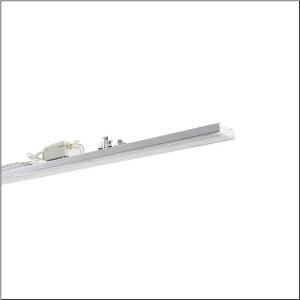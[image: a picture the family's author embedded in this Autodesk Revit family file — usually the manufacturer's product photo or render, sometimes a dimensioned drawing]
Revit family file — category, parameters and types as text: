
# Revit family: licross_r__21_recessed_mo_52tl12de45xg_f928
name_source: partatom
category: Lighting Fixtures
units: mm (PartAtom-declared; Revit-internal decimal feet)

## family parameters
Cut with Voids When Loaded = No
Host = Face
Light Source = No
Part Type = Normal
Room Calculation Point = No
Round Connector Dimension = Use Diameter
Shared = No

## types (1)
- --- (1 x LED, 5140 lm, 29.9 W, 4000K)
    Apparent Load = 30 VA
    CIE Flux Codes = 72 92 99 100 100
    Color Rendering = 80
    Color Temperature = 4000K
    Default Elevation = 1800 mm
    Description = Licross® 21 Recessed MO, luminaire insert, of sheet steel, galvanised, coil coated, white, length: 750mm, width: 66mm, height: 67mm, LED rated luminous flux: 5.140lm, light colour: 840, control gear: DALI 2, with plug, 5-pole, with phase selection, mains connection: 220..240V, AC, 50/60Hz, rated input power: 30W, halogen-free wiring, primary light control with lens, of plastic, primary optical cover: cover, of PMMA, light emission: direct distribution, primary light characteristic: symmetric, protection rating (complete): IP40, insulation class (complete): insulation class I (protective earthing), certification: CE, ENEC, VDE, UKCA, protection symbol: D if used in an environment without relevant dust loads with corresponding accessories, impact resistance: IK06, permissible ambient temperature for indoor applications: -25..+35°C, corresponds to IFS (International Featured Standards) requirements for safety and quality in the food industry, reducing of maximum allowable ambient temperature of 5°C with ceiling mounting, LABS conformity tested according to VDMA 24364:2018-05, packaging unit: 1 piece
    Height = 58 mm
    Lamp = 1 x LED
    Lamp Light Flux = 5140 lm
    Lamp Power = 29.9 W
    Lamp count = 1
    Length = 750 mm
    Luminous efficacy = 172 lm/W
    Manufacturer = Siteco
    ModVariant = No
    Model = 52TL12DE45XG
    Mounting Place = Ceiling
    Mounting Type = Pendant
    Number of Poles = 1
    OnlyDefault = Yes
    Power Factor = 1
    Product Name = Licross® 21 Recessed MO
    Product group = luminaire insert
    ProductGroupID = 901
    Protection Class = Protection class I
    Protection Degree = IP 40
    RLX_Detail_Level = 1
    RLX_Emergency_Light_Flux = 0 lm
    RLX_Emergency_Type = 0
    RLX_Emergency_Type_DB = No
    RlxData = <blob elided: 28765 chars, md5=e0859f14>
    Socket = socket
    Standby Power = 0 W
    System Light Flux = 5140 lm
    System Power = 30 W
    Type Comments = factory setting: luminous flux: 100 % | dim-lin: 254 | 390 mA
    Type Image = l_1296930.jpg
    URL = http://relux.com
    VarID = @adj_058073
    Voltage = 0 V
    Weight = 0.00 kg
    Width = 66 mm

## geometry (parser evidence)
native form markers: Blend x4, Sweep x12
no freeform markers — native parametric forms only
